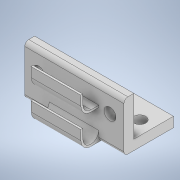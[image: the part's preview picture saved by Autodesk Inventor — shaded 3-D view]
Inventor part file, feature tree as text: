
AUTODESK INVENTOR PART (.ipt)
format: ipt  version: 2020 (Build 240168000, 168)  size: 223,232 bytes
history: native  units: in
note: dims shown in document units (in); Inventor stores cm internally (conversion verified against a paired STEP export)
features: extrude x8, sketch x8, direct_edit x1, plane x1, fillet x1, move_body x1
ambient origin geometry x8: Origin, YZ Plane, XZ Plane, XY Plane, X Axis, Y Axis, Z Axis, Center Point
bodies: Solid1 (feature_tree)
feature tree (20):
  extrude  "Extrusion1"  Depth=0.9843in
  extrude  "Extrusion2"  Depth=0.1969in
  extrude  "Extrusion3"  Depth=0.2362in
  extrude  "Extrusion4"  Depth=0.2362in
  direct_edit  "Direct Edit1"
  extrude  "Extrusion5"  Depth=0.3937in
  extrude  "Extrusion6"  Depth=0.9843in TaperAngle=0.0deg
  extrude  "Extrusion7"  Depth=0.2756in
  plane  "Work Plane1"
  sketch  "Sketch8"  dims[d21=0.2362in d22=0.2756in d23=0.0in d24=0.0in d25=0.2362in d26=0.2756in d27=0.0in d28=0.0in d29=0.9843in d30=0.3937in d31=0.0in d45=0.3937in d58=0.0787in d60=0.315in d61=0.1575in d62=0.1969in d64=0.315in d65=0.1575in d66=0.1969in d70=0.6322in d71=0.6322in d72=0.6322in d73=0.6322in d74=0.0in d75=0.0in d48=0.0197in d49=0.0344in d50=0.0197in d51=0.0344in d67=0.0197in d68=0.0344in d69=0.0197in]
  extrude  "Extrusion13"  Depth=0.1969in
  fillet  "Fillet3"  [1 undecoded]
  sketch  "Sketch1"  dims[d0=0.9843in d1=0.9843in]
  sketch  "Sketch2"  dims[d2=0.1969in d3=0.0in d4=0.1969in]
  sketch  "Sketch3"  dims[d5=0.7874in d6=0.0in d8=0.2362in]
  sketch  "Sketch4"  dims[d9=0.0in d10=0.0in d11=0.2362in]
  sketch  "Sketch5"  dims[d12=0.3937in d13=0.3937in]
  sketch  "Sketch6"  dims[d14=0.0in d15=0.0in d16=0.0in d17=0.0in d18=0.9843in]
  sketch  "Sketch7"  dims[d19=0.2756in d20=0.2756in]
  move_body  "Move1"
note: 1 required parameter value undecoded (feature->parameter linkage not recoverable at this tier; creation-order binding heuristic only, values carry confidence <= 0.55)
